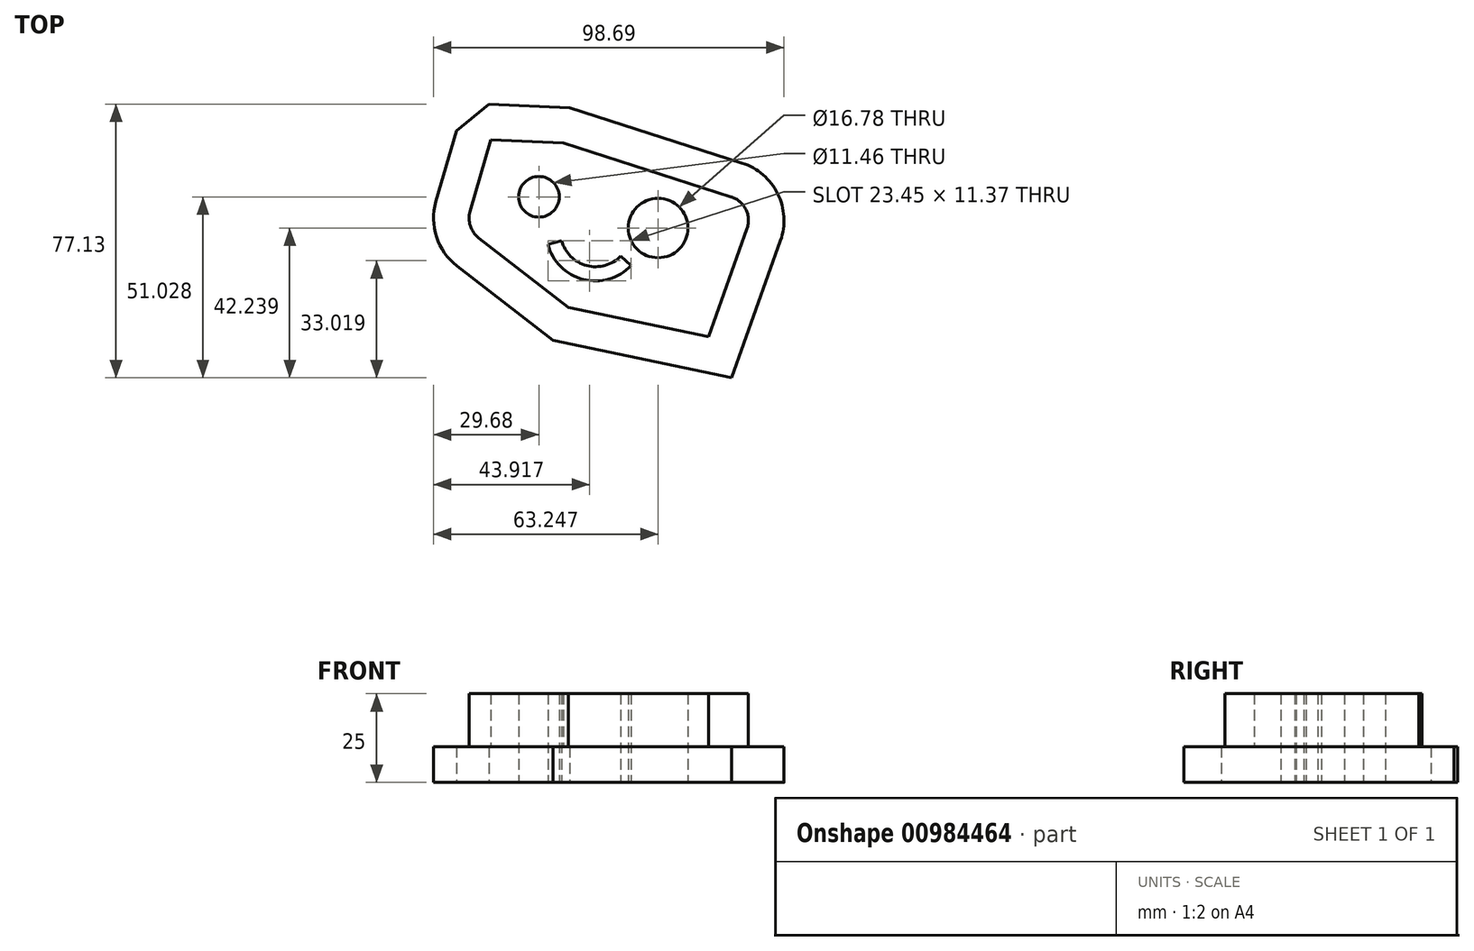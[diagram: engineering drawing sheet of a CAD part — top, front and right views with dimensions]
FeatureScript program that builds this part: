
annotation { "Feature Type Name" : "Feature", "Feature Type Description" : "" }
export const myFeature = defineFeature(function(context is Context, id is Id, definition is map)
    precondition{}
    {
        {
            var Q0;
            Q0=qCreatedBy(makeId("Top.planeOp"),FACE);
            var sketch = newSketch(context, id + "F0", { "sketchPlane" : qUnion([Q0])});
            skLineSegment(sketch, "E0", {"start": v(-32.74, 29.4) * mm, "end": v(-38.63, 9.26) * mm});
            skLineSegment(sketch, "E1", {"start": v(-36.2, 1.76) * mm, "end": v(-10.9, -17.8) * mm});
            skLineSegment(sketch, "E2", {"start": v(-10.9, -17.8) * mm, "end": v(28.57, -26.1) * mm});
            skLineSegment(sketch, "E3", {"start": v(28.57, -26.1) * mm, "end": v(39.37, 4.33) * mm});
            skLineSegment(sketch, "E4", {"start": v(34.92, 13.34) * mm, "end": v(-12.4, 28.54) * mm});
            skLineSegment(sketch, "E5", {"start": v(-12.4, 28.54) * mm, "end": v(-32.74, 29.4) * mm});
            skLineSegment(sketch, "E6", {"start": v(-12.4, 28.54) * mm, "end": v(1.84, -20.48) * mm, "construction": true});
            skPoint(sketch, "E7.visualSharp", {"position": v(-39.97, 4.68) * mm});
            skArc(sketch, "E7.filletArc", {"start": v(-38.63, 9.26) * mm, "mid": v(-38.57, 5.13) * mm, "end": v(-36.2, 1.76) * mm});
            skPoint(sketch, "E8.visualSharp", {"position": v(41.78, 11.13) * mm});
            skArc(sketch, "E8.filletArc", {"start": v(39.37, 4.33) * mm, "mid": v(39.05, 9.78) * mm, "end": v(34.92, 13.34) * mm});
            skLineSegment(sketch, "E9.0", {"start": v(-10.62, 38.47) * mm, "end": v(-33.34, 39.44) * mm});
            skLineSegment(sketch, "E9.1", {"start": v(37.98, 22.86) * mm, "end": v(-10.62, 38.47) * mm});
            skLineSegment(sketch, "E9.2", {"start": v(-42.3, -6.15) * mm, "end": v(-15.2, -27.11) * mm});
            skLineSegment(sketch, "E9.3", {"start": v(-15.2, -27.11) * mm, "end": v(35.07, -37.7) * mm});
            skLineSegment(sketch, "E9.4", {"start": v(35.07, -37.7) * mm, "end": v(48.8, 0.99) * mm});
            skArc(sketch, "E9.5", {"start": v(48.8, 0.99) * mm, "mid": v(48.01, 14.21) * mm, "end": v(37.98, 22.86) * mm});
            skArc(sketch, "E10.0", {"start": v(-48.23, 12.06) * mm, "mid": v(-48.08, 2.04) * mm, "end": v(-42.3, -6.15) * mm});
            skLineSegment(sketch, "E10.1", {"start": v(-42.4, 31.97) * mm, "end": v(-48.23, 12.06) * mm});
            skLineSegment(sketch, "E11", {"start": v(-42.4, 31.97) * mm, "end": v(-33.34, 39.44) * mm});
            skCircle(sketch, "E12", {"center": v(-19.23, 13.34) * mm, "radius": 5.73 * mm});
            skCircle(sketch, "E13", {"center": v(14.34, 4.55) * mm, "radius": 8.4 * mm});
            skArc(sketch, "E14", {"start": v(-16.72, 0) * mm, "mid": v(-6.77, -9.91) * mm, "end": v(6.73, -6.07) * mm});
            skArc(sketch, "E15.0", {"start": v(-12.85, 1.01) * mm, "mid": v(-5.77, -6.04) * mm, "end": v(3.84, -3.3) * mm});
            skLineSegment(sketch, "E16", {"start": v(-16.72, 0) * mm, "end": v(-12.85, 1.01) * mm});
            skLineSegment(sketch, "E17", {"start": v(3.84, -3.3) * mm, "end": v(6.73, -6.07) * mm});
            skSolve(sketch);
        }
        {
            var Q0;
            Q0=makeQuery(id+"F0.imprint","IMPRINT",FACE,{"disambiguationData":[TD([[makeQuery(id+"F0.imprint","IMPRINT",EDGE,{"derivedFrom":sQuery(id+"F0.wireOp",EDGE,"E0")}),1.0]])]});
            extrude(context, id + "F1", {"entities" : qUnion([Q0]), "depth" : 25 * mm, "offsetDistance" : 25 * mm});
        }
        {
            var Q0;
            Q0 = qSketchRegion(id + "F0", true);
            extrude(context, id + "F2", {"entities" : qUnion([Q0]), "operationType" : NewBodyOperationType.ADD, "depth" : 10 * mm, "offsetDistance" : 25 * mm});
        }
    });
